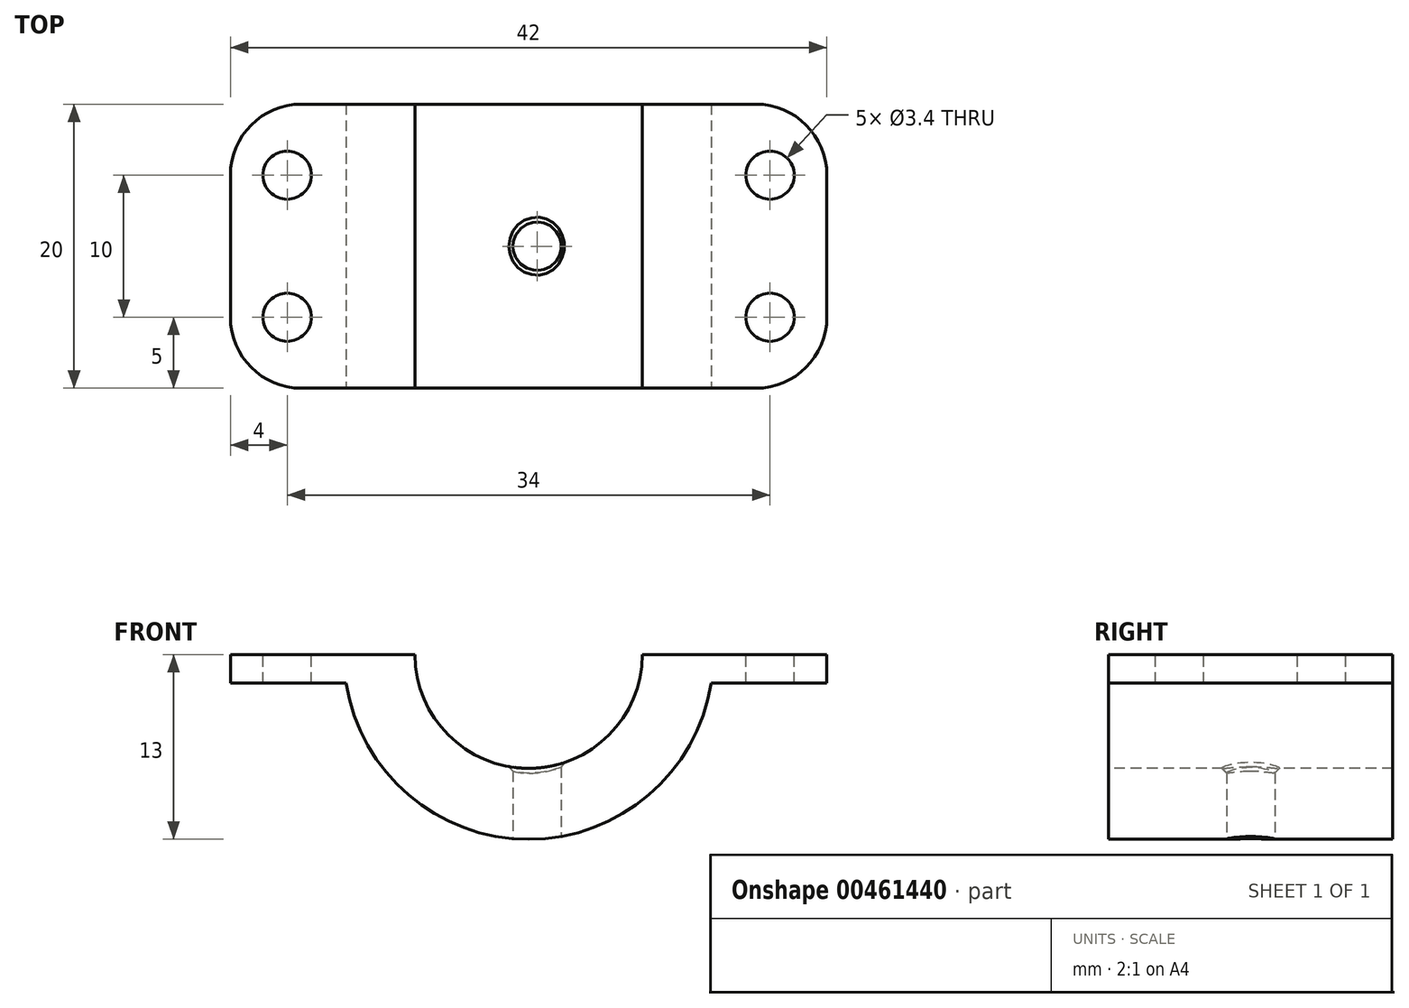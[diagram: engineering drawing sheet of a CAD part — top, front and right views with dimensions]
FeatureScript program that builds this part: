
annotation { "Feature Type Name" : "Feature", "Feature Type Description" : "" }
export const myFeature = defineFeature(function(context is Context, id is Id, definition is map)
    precondition{}
    {
        {
            var Q0;
            Q0=qCreatedBy(makeId("Top.planeOp"),FACE);
            var sketch = newSketch(context, id + "F0", { "sketchPlane" : qUnion([Q0])});
            skLineSegment(sketch, "E0.bottom", {"start": v(0, 0) * mm, "end": v(55, 0) * mm});
            skLineSegment(sketch, "E0.top", {"start": v(0, -20) * mm, "end": v(55, -20) * mm});
            skLineSegment(sketch, "E0.left", {"start": v(0, 0) * mm, "end": v(0, -20) * mm});
            skLineSegment(sketch, "E0.right", {"start": v(55, 0) * mm, "end": v(55, -20) * mm});
            skSolve(sketch);
        }
        {
            var Q0;
            Q0 = qSketchRegion(id + "F0", true);
            extrude(context, id + "F1", {"entities" : qUnion([Q0]), "depth" : 13 * mm});
        }
        {
            var Q0;
            Q0=makeQuery(id+"F1.opExtrude","SWEPT_FACE",FACE,{"disambiguationData":[OSD([sQuery(id+"F0.wireOp",EDGE,"E0.top")])]});
            var sketch = newSketch(context, id + "F2", { "sketchPlane" : qUnion([Q0])});
            skLineSegment(sketch, "E1", {"start": v(27.5, 0) * mm, "end": v(27.5, 13) * mm});
            skCircle(sketch, "E2", {"center": v(27.5, 13) * mm, "radius": 8 * mm});
            skLineSegment(sketch, "E3", {"start": v(27.5, 13) * mm, "end": v(35.5, 13) * mm});
            skCircle(sketch, "E4.0", {"center": v(27.5, 13) * mm, "radius": 13 * mm});
            skSolve(sketch);
        }
        {
            var Q0;
            {var subQ1=sQuery(id+"F0.wireOp",EDGE,"E0.top");var subQ6=makeQuery(id+"F1.opExtrude","SWEPT_EDGE",EDGE,{"disambiguationData":[OSD([subQ1,sQuery(id+"F0.wireOp",EDGE,"E0.left")])]});Q0=makeQuery(id+"F2.imprint","IMPRINT",FACE,{"disambiguationData":[TD([[makeQuery(id+"F2.imprint","IMPRINT",EDGE,{"derivedFrom":subQ6}),1.0]])]});}
            var Q1;
            {var subQ1=sQuery(id+"F0.wireOp",EDGE,"E0.top");var subQ6=makeQuery(id+"F1.opExtrude","SWEPT_EDGE",EDGE,{"disambiguationData":[OSD([subQ1,sQuery(id+"F0.wireOp",EDGE,"E0.right")])]});Q1=makeQuery(id+"F2.imprint","IMPRINT",FACE,{"disambiguationData":[TD([[makeQuery(id+"F2.imprint","IMPRINT",EDGE,{"derivedFrom":subQ6}),-1.0]])]});}
            var Q2;
            {var subQ0=sQuery(id+"F2.wireOp",EDGE,"E3");Q2=makeQuery(id+"F2.imprint","IMPRINT",FACE,{"disambiguationData":[TD([[makeQuery(id+"F2.imprint","IMPRINT",EDGE,{"derivedFrom":subQ0}),-1.0]])]});}
            var Q3;
            {var subQ0=sQuery(id+"F2.wireOp",EDGE,"E1");var subQ3=sQuery(id+"F2.wireOp",EDGE,"E2");var subQ4=makeQuery(id+"F2.imprint","INTERSECT",VERTEX,{"derivedFrom":[subQ0,subQ3]});Q3=makeQuery(id+"F2.imprint","IMPRINT",FACE,{"disambiguationData":[TD([[makeQuery(id+"F2.imprint","IMPRINT",EDGE,{"disambiguationData":[TD([[subQ4,1.0]])],"derivedFrom":subQ3}),1.0]])]});}
            extrude(context, id + "F3", {"entities" : qUnion([Q0, Q1, Q2, Q3]), "operationType" : NewBodyOperationType.REMOVE, "oppositeDirection" : true, "depth" : 20 * mm});
        }
        {
            var Q0;
            Q0=makeQuery(id+"F3.boolean.opBoolean","SPLIT",FACE,{"disambiguationData":[OD(1.0)],"derivedFrom":makeQuery(id+"F1.opExtrude","CAP_FACE",FACE,{"disambiguationData":[OSD([sQuery(id+"F0.wireOp",EDGE,"E0.bottom"),sQuery(id+"F0.wireOp",EDGE,"E0.top"),sQuery(id+"F0.wireOp",EDGE,"E0.left"),sQuery(id+"F0.wireOp",EDGE,"E0.right")])],"isStart":false})});
            var sketch = newSketch(context, id + "F4", { "sketchPlane" : qUnion([Q0])});
            skPoint(sketch, "E5.oppositeSnap0", {"position": v(17, -20) * mm});
            skLineSegment(sketch, "E5.bottom", {"start": v(19.5, 0) * mm, "end": v(6.5, 0) * mm});
            skLineSegment(sketch, "E5.top", {"start": v(19.5, -20) * mm, "end": v(6.5, -20) * mm});
            skLineSegment(sketch, "E5.left", {"start": v(19.5, 0) * mm, "end": v(19.5, -20) * mm});
            skLineSegment(sketch, "E5.right", {"start": v(6.5, 0) * mm, "end": v(6.5, -20) * mm});
            skLineSegment(sketch, "E6", {"start": v(19.5, 0) * mm, "end": v(35.5, 0) * mm});
            skLineSegment(sketch, "E7.bottom", {"start": v(35.5, 0) * mm, "end": v(48.5, 0) * mm});
            skLineSegment(sketch, "E7.top", {"start": v(35.5, -20) * mm, "end": v(48.5, -20) * mm});
            skLineSegment(sketch, "E7.left", {"start": v(35.5, 0) * mm, "end": v(35.5, -20) * mm});
            skLineSegment(sketch, "E7.right", {"start": v(48.5, 0) * mm, "end": v(48.5, -20) * mm});
            skSolve(sketch);
        }
        {
            var Q0;
            Q0 = qSketchRegion(id + "F4", true);
            extrude(context, id + "F5", {"entities" : qUnion([Q0]), "operationType" : NewBodyOperationType.ADD, "oppositeDirection" : true, "depth" : 2 * mm});
        }
        {
            var Q0;
            Q0=makeQuery(id+"F5.opExtrude","SWEPT_EDGE",EDGE,{"disambiguationData":[OSD([sQuery(id+"F4.wireOp",EDGE,"E7.top"),sQuery(id+"F4.wireOp",EDGE,"E7.right")])]});
            var Q1;
            Q1=makeQuery(id+"F5.opExtrude","SWEPT_EDGE",EDGE,{"disambiguationData":[OSD([sQuery(id+"F4.wireOp",EDGE,"E7.bottom"),sQuery(id+"F4.wireOp",EDGE,"E7.right")])]});
            var Q2;
            Q2=makeQuery(id+"F5.opExtrude","SWEPT_EDGE",EDGE,{"disambiguationData":[OSD([sQuery(id+"F4.wireOp",EDGE,"E5.top"),sQuery(id+"F4.wireOp",EDGE,"E5.right")])]});
            var Q3;
            Q3=makeQuery(id+"F5.opExtrude","SWEPT_EDGE",EDGE,{"disambiguationData":[OSD([sQuery(id+"F4.wireOp",EDGE,"E5.bottom"),sQuery(id+"F4.wireOp",EDGE,"E5.right")])]});
            fillet(context, id + "F6", {"entities" : qUnion([Q0, Q1, Q2, Q3]), "radius" : 5 * mm, "tangentPropagation" : true, "allowEdgeOverflow" : false});
        }
        {
            var Q0;
            Q0=makeQuery(id+"F5.boolean.opBoolean","MERGE",FACE,{"derivedFrom":[makeQuery(id+"F3.boolean.opBoolean","SPLIT",FACE,{"disambiguationData":[OD(1.0)],"derivedFrom":makeQuery(id+"F1.opExtrude","CAP_FACE",FACE,{"disambiguationData":[OSD([sQuery(id+"F0.wireOp",EDGE,"E0.bottom"),sQuery(id+"F0.wireOp",EDGE,"E0.top"),sQuery(id+"F0.wireOp",EDGE,"E0.left"),sQuery(id+"F0.wireOp",EDGE,"E0.right")])],"isStart":false})}),makeQuery(id+"F5.opExtrude","CAP_FACE",FACE,{"disambiguationData":[OSD([sQuery(id+"F4.wireOp",EDGE,"E5.bottom"),sQuery(id+"F4.wireOp",EDGE,"E5.top"),sQuery(id+"F4.wireOp",EDGE,"E5.left"),sQuery(id+"F4.wireOp",EDGE,"E5.right")])],"isStart":true})]});
            var sketch = newSketch(context, id + "F7", { "sketchPlane" : qUnion([Q0])});
            skLineSegment(sketch, "E8", {"start": v(6.5, -10) * mm, "end": v(10.5, -10) * mm});
            skLineSegment(sketch, "E9", {"start": v(10.5, -10) * mm, "end": v(10.5, -5) * mm});
            skLineSegment(sketch, "E10", {"start": v(10.5, -10) * mm, "end": v(10.5, -15) * mm});
            skCircle(sketch, "E11", {"center": v(10.5, -5) * mm, "radius": 1.7 * mm});
            skCircle(sketch, "E12", {"center": v(10.5, -15) * mm, "radius": 1.7 * mm});
            skLineSegment(sketch, "E13", {"start": v(19.5, 0) * mm, "end": v(27.5, 0) * mm});
            skLineSegment(sketch, "E14", {"start": v(27.5, 0) * mm, "end": v(27.5, -18.28) * mm});
            skLineSegment(sketch, "E15.MirrorCS", {"start": v(44.5, -10) * mm, "end": v(44.5, -5) * mm});
            skLineSegment(sketch, "E16.MirrorCS", {"start": v(48.5, -10) * mm, "end": v(44.5, -10) * mm});
            skLineSegment(sketch, "E17.MirrorCS", {"start": v(44.5, -10) * mm, "end": v(44.5, -15) * mm});
            skCircle(sketch, "E18.MirrorC", {"center": v(44.5, -5) * mm, "radius": 1.7 * mm});
            skCircle(sketch, "E19.MirrorC", {"center": v(44.5, -15) * mm, "radius": 1.7 * mm});
            skSolve(sketch);
        }
        {
            var Q0;
            Q0 = qSketchRegion(id + "F7", true);
            extrude(context, id + "F8", {"entities" : qUnion([Q0]), "operationType" : NewBodyOperationType.REMOVE, "oppositeDirection" : true, "depth" : 2 * mm});
        }
        {
            var Q0;
            Q0=qCreatedBy(makeId("Top.planeOp"),FACE);
            var sketch = newSketch(context, id + "F9", { "sketchPlane" : qUnion([Q0])});
            skLineSegment(sketch, "E20", {"start": v(0, 0) * mm, "end": v(27.5, 0) * mm});
            skLineSegment(sketch, "E21", {"start": v(27.5, 0) * mm, "end": v(27.5, -10) * mm});
            skCircle(sketch, "E22", {"center": v(28.1, -10) * mm, "radius": 1.7 * mm});
            skSolve(sketch);
        }
        {
            var Q0;
            Q0 = qSketchRegion(id + "F9", true);
            extrude(context, id + "F10", {"entities" : qUnion([Q0]), "operationType" : NewBodyOperationType.REMOVE, "depth" : 6 * mm});
        }
        {
            var Q0;
            Q0=makeQuery(id+"F8.boolean.opBoolean","COPY",EDGE,{"derivedFrom":makeQuery(id+"F8.opExtrude","CAP_EDGE",EDGE,{"disambiguationData":[OSD([sQuery(id+"F7.wireOp",EDGE,"E11")])],"isStart":true})});
            var Q1;
            Q1=makeQuery(id+"F8.boolean.opBoolean","COPY",EDGE,{"derivedFrom":makeQuery(id+"F8.opExtrude","CAP_EDGE",EDGE,{"disambiguationData":[OSD([sQuery(id+"F7.wireOp",EDGE,"E12")])],"isStart":true})});
            var Q2;
            Q2=makeQuery(id+"F8.boolean.opBoolean","COPY",EDGE,{"derivedFrom":makeQuery(id+"F8.opExtrude","CAP_EDGE",EDGE,{"disambiguationData":[OSD([sQuery(id+"F7.wireOp",EDGE,"E12")])],"isStart":false})});
            var Q3;
            Q3=makeQuery(id+"F8.boolean.opBoolean","COPY",EDGE,{"derivedFrom":makeQuery(id+"F8.opExtrude","CAP_EDGE",EDGE,{"disambiguationData":[OSD([sQuery(id+"F7.wireOp",EDGE,"E11")])],"isStart":false})});
            var Q4;
            Q4=makeQuery(id+"F8.boolean.opBoolean","COPY",EDGE,{"derivedFrom":makeQuery(id+"F8.opExtrude","CAP_EDGE",EDGE,{"disambiguationData":[OSD([sQuery(id+"F7.wireOp",EDGE,"E19.MirrorC")])],"isStart":true})});
            var Q5;
            Q5=makeQuery(id+"F8.boolean.opBoolean","COPY",EDGE,{"derivedFrom":makeQuery(id+"F8.opExtrude","CAP_EDGE",EDGE,{"disambiguationData":[OSD([sQuery(id+"F7.wireOp",EDGE,"E19.MirrorC")])],"isStart":false})});
            var Q6;
            Q6=makeQuery(id+"F8.boolean.opBoolean","COPY",EDGE,{"derivedFrom":makeQuery(id+"F8.opExtrude","CAP_EDGE",EDGE,{"disambiguationData":[OSD([sQuery(id+"F7.wireOp",EDGE,"E18.MirrorC")])],"isStart":true})});
            var Q7;
            Q7=makeQuery(id+"F8.boolean.opBoolean","COPY",EDGE,{"derivedFrom":makeQuery(id+"F8.opExtrude","CAP_EDGE",EDGE,{"disambiguationData":[OSD([sQuery(id+"F7.wireOp",EDGE,"E18.MirrorC")])],"isStart":false})});
            var Q8;
            Q8=makeQuery(id+"F10.boolean.opBoolean","INTERSECT",EDGE,{"derivedFrom":[makeQuery(id+"F3.boolean.opBoolean","COPY",FACE,{"derivedFrom":makeQuery(id+"F3.opExtrude","SWEPT_FACE",FACE,{"disambiguationData":[OSD([sQuery(id+"F2.wireOp",EDGE,"E2")])]})}),makeQuery(id+"F10.opExtrude","SWEPT_FACE",FACE,{"disambiguationData":[OSD([sQuery(id+"F9.wireOp",EDGE,"E22")])]})]});
            var Q9;
            {var subQ0=sQuery(id+"F2.wireOp",EDGE,"E4.0");var subQ1=sQuery(id+"F0.wireOp",EDGE,"E0.top");var subQ3=makeQuery(id+"F1.opExtrude","CAP_EDGE",EDGE,{"disambiguationData":[OSD([subQ1])],"isStart":false});Q9=makeQuery(id+"F10.boolean.opBoolean","INTERSECT",EDGE,{"derivedFrom":[makeQuery(id+"F3.boolean.opBoolean","TWEAK_FACE",FACE,{"derivedFrom":[makeQuery(id+"F3.opExtrude","SWEPT_FACE",FACE,{"disambiguationData":[OSD([subQ0]),TDD([makeQuery(id+"F2.imprint","IMPRINT",EDGE,{"disambiguationData":[TD([[makeQuery(id+"F2.imprint","INTERSECT",VERTEX,{"disambiguationData":[OD(0.0)],"derivedFrom":[subQ3,subQ0]}),-1.0]])],"derivedFrom":subQ0})])]}),makeQuery(id+"F3.opExtrude","SWEPT_FACE",FACE,{"disambiguationData":[OSD([subQ0]),TDD([makeQuery(id+"F2.imprint","IMPRINT",EDGE,{"disambiguationData":[TD([[makeQuery(id+"F2.imprint","INTERSECT",VERTEX,{"disambiguationData":[OD(1.0)],"derivedFrom":[subQ3,subQ0]}),1.0]])],"derivedFrom":subQ0})])]})]}),makeQuery(id+"F10.opExtrude","SWEPT_FACE",FACE,{"disambiguationData":[OSD([sQuery(id+"F9.wireOp",EDGE,"E22")])]})]});}
            chamfer(context, id + "F11", {"entities" : qUnion([Q0, Q1, Q2, Q3, Q4, Q5, Q6, Q7, Q8, Q9]), "width" : 0.34 * mm, "tangentPropagation" : true});
        }
    });
